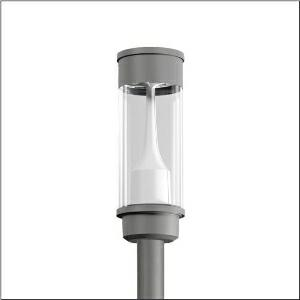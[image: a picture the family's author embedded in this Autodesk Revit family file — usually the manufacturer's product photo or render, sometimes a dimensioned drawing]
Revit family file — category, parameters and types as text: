
# Revit family: litepole_iq___p1_0a_5xa5415lf14h_d8b4
name_source: partatom
category: Lighting Fixtures
units: mm (PartAtom-declared; Revit-internal decimal feet)

## family parameters
Cut with Voids When Loaded = No
Host = Face
Light Source = No
Part Type = Normal
Room Calculation Point = No
Round Connector Dimension = Use Diameter
Shared = No

## types (1)
- --- (1 x LED, 1510 lm, 10 W, 4000K)
    Apparent Load = 10 VA
    CIE Flux Codes = 32 61 90 93 100
    Color Rendering = 70
    Color Temperature = 4000K
    Default Elevation = 1800 mm
    Description = Litepole iQ, mast luminaire, Module 540 iQ-SR, primary light control with 3 zone facetted reflector, of plastic, silver coated, highly specular, structured, primary optical cover: cover, of PMMA, transparent, partly coated, light distribution: P1.0a, light emission: direct distribution, primary light characteristic: strongly asymmetric, installation type: post-top, LED, High Power LED, rated luminous flux: 1.510lm, luminous efficacy: 151lm/W, light colour: 740, colour temperature: 4000K, control gear: ECG iQ, control: optimised constant luminous flux control (CLO 2.0), Desk-Remote (wireless, voltage-free reading and setting of iQ features in the workshop via application-optimized NFC function/RFID function), Light-Fading, Smart-Wire, Night-Set, Lumen-Switch, Temp-Guard, Auto-Match, Street-Remote, presetting dimming logarithmic, with terminal, 6-pole, max. 2.5mm², mains connection: 220..240V, AC, 50/60Hz, start of lifetime: 10W, end of lifetime: 10W, reduction: 5W, luminaire housing, upper part, of glass-fibre reinforced polyester, coated, Siteco® metallic grey (DB 702S), diameter: 210mm, height: 590mm, spigot size: d x l = 76 x 70mm (post-top) | with reducer (optional accessory) 60 x 70mm, post-top mast mounting element, of diecast aluminium, coated, Siteco® metallic grey (DB 702S), Module 540 iQ-SR, traffic white (RAL 9016), equipment: standard, protection rating (complete): IP65, insulation class (complete): insulation class II (safety insulation), certification: CE, ENEC, VDE, packaging unit: 1 piece

Light Distribution: P1.0a
    Height = 590 mm
    Lamp = 1 x LED
    Lamp Light Flux = 1510 lm
    Lamp Power = 10 W
    Lamp count = 1
    Length = 220 mm
    Luminous efficacy = 151 lm/W
    Manufacturer = Siteco
    ModVariant = No
    Model = 5XA5415LF14H
    Number of Poles = 1
    OnlyDefault = Yes
    Power Factor = 1
    Product Name = Litepole iQ | P1.0a
    Product group = mast luminaire | pylon top
    ProductGroupID = 6100
    Protection Class = Protection class II
    Protection Degree = IP 65
    RLX_Detail_Level = 1
    RlxData = <blob elided: 68157 chars, md5=0c3c682c>
    Socket = socket
    Standby Power = 0 W
    System Light Flux = 1510 lm
    System Power = 10 W
    Type Comments = factory setting: luminous flux: 100 % | dim-lin: 254 | 401 mA
    Type Image = l_1006025.jpg
    URL = http://relux.com
    VarID = @adj_069943
    Voltage = 0 V
    Weight = 0.00 kg
    Width = 0 mm  [stored 0 ft]

note: [stored X ft] marks values corroborated as IEEE doubles in the binary element streams (Revit-internal decimal feet)

## geometry (parser evidence)
native form markers: Blend x4, Sweep x12
no freeform markers — native parametric forms only
